FCSTD DOCUMENT  (FreeCAD 0.16R5861 (Git))
Label: flexystruder_body_holderV0.4
License: CreativeCommons Attribution-ShareAlike
LicenseURL: http://creativecommons.org/licenses/by-sa/4.0/
objects: Sketcher::SketchObject×9, PartDesign::Pad×6, Part::Feature×4, PartDesign::Pocket×3, Mesh::Feature×1, PartDesign::Chamfer×1, Part::Cut×1, PartDesign::Fillet×1
note: 34 computed .brp shape members not serialized (recipe doc carries the construction recipe); baked Part::Feature solids carry a one-line shape summary decoded from their .brp

FEATURE [Mesh::Feature] flexystruder_body_hex_v2_0  label="flexystruder_body_hex_v2.0"
FEATURE [Part::Feature] flexystruder_body_hex_v2_0001
  shape: bbox 97.06 x 64.55 x 27.5 mm, 7934 faces, 0 solids (baked)
FEATURE [Part::Feature] flexystruder_body_hex_v2_0001001  label="flexystruder_body_hex_v2_0002"
  shape: bbox 97.06 x 64.55 x 27.5 mm, 4378 faces, 0 solids (baked)
FEATURE [Part::Feature] flexystruder_body_hex_v2_0001001_solid  label="flexystruder_body_hex_v2_0002 (Solid)"
  shape: bbox 97.06 x 64.55 x 27.5 mm, 4378 faces (baked)
FEATURE [Sketcher::SketchObject] Sketch
  Placement = pos=(0,0,0) rot=(1,0,0;3.14159rad)
  Support = -> flexystruder_body_hex_v2_0001001_solid [Face1922]
  sketch-geometry (17):
    g0: ArcOfCircle CenterX=28 CenterY=-45.596 CenterZ=0 NormalX=0 NormalY=0 NormalZ=1 Radius=4.20615 StartAngle=4.71239 EndAngle=7.85398
    g1: ArcOfCircle CenterX=25 CenterY=-45.596 CenterZ=0 NormalX=0 NormalY=0 NormalZ=1 Radius=4.20615 StartAngle=1.5708 EndAngle=4.71239
    g2: LineSegment StartX=28 StartY=-41.3899 StartZ=0 EndX=25 EndY=-41.3899 EndZ=0
    g3: LineSegment StartX=28 StartY=-49.8022 StartZ=0 EndX=25 EndY=-49.8022 EndZ=0
    g4: ArcOfCircle CenterX=52.7327 CenterY=-58.2604 CenterZ=0 NormalX=0 NormalY=0 NormalZ=1 Radius=4.37439 StartAngle=1.5708 EndAngle=4.71239
    g5: ArcOfCircle CenterX=55.547 CenterY=-58.2604 CenterZ=0 NormalX=0 NormalY=0 NormalZ=1 Radius=4.37439 StartAngle=4.71239 EndAngle=7.85398
    g6: LineSegment StartX=52.7327 StartY=-62.6347 StartZ=0 EndX=55.547 EndY=-62.6347 EndZ=0
    g7: LineSegment StartX=52.7327 StartY=-53.886 StartZ=0 EndX=55.547 EndY=-53.886 EndZ=0
    g8: ArcOfCircle CenterX=41 CenterY=-17.6915 CenterZ=0 NormalX=0 NormalY=0 NormalZ=1 Radius=4.05397 StartAngle=4.71239 EndAngle=7.85398
    g9: ArcOfCircle CenterX=37.752 CenterY=-17.6915 CenterZ=0 NormalX=0 NormalY=0 NormalZ=1 Radius=4.05397 StartAngle=1.5708 EndAngle=4.71239
    g10: LineSegment StartX=41 StartY=-13.6375 StartZ=0 EndX=37.752 EndY=-13.6375 EndZ=0
    g11: LineSegment StartX=41 StartY=-21.7455 StartZ=0 EndX=37.752 EndY=-21.7455 EndZ=0
    g12: LineSegment StartX=23.6875 StartY=-6 StartZ=0 EndX=35.6731 EndY=-6 EndZ=0
    g13: LineSegment StartX=16.4026 StartY=-28 StartZ=0 EndX=28.3058 EndY=-28 EndZ=0
    g14: LineSegment StartX=28.3058 StartY=-28 StartZ=0 EndX=35.6731 EndY=-6 EndZ=0
    g15: LineSegment StartX=16.4026 StartY=-28 StartZ=0 EndX=16.4026 EndY=-12.5849 EndZ=0
    g16: ArcOfCircle CenterX=23.5917 CenterY=-13.2161 CenterZ=0 NormalX=0 NormalY=0 NormalZ=1 Radius=7.21677 StartAngle=1.55753 EndAngle=3.05401
  constraints (26):
    c: Tangent(g0,g3) = 1.5708
    c: Tangent(g0,g2) = -1.5708
    c: Tangent(g2,g1) = -1.5708
    c: Tangent(g3,g1) = 1.5708
    c: Horizontal(g2)
    c: Equal(g0,g1)
    c: Tangent(g4,g7) = 1.5708
    c: Tangent(g4,g6) = -1.5708
    c: Tangent(g6,g5) = -1.5708
    c: Tangent(g7,g5) = 1.5708
    c: Horizontal(g6)
    c: Equal(g4,g5)
    c: Tangent(g8,g11) = 1.5708
    c: Tangent(g8,g10) = -1.5708
    c: Tangent(g10,g9) = -1.5708
    c: Tangent(g11,g9) = 1.5708
    c: Horizontal(g10)
    c: Equal(g8,g9)
    c: Horizontal(g12)
    c: Horizontal(g13)
    c: Coincident(g14,g13)
    c: Coincident(g14,g12)
    c: Coincident(g15,g13)
    c: Vertical(g15)
    c: Coincident(g16,g12)
    c: Coincident(g16,g15)
FEATURE [PartDesign::Pad] Pad
  Length = 9.5
  Length2 = 100
  Reversed = true
  Sketch = -> Sketch
  Type = 0
FEATURE [Sketcher::SketchObject] Sketch001
  ExternalGeometry = -> [Pad]
  Placement = pos=(17.5,0,0) rot=(0.57735,0.57735,0.57735;2.0944rad)
  Support = -> Pad [Face375]
  sketch-geometry (4):
    g0: LineSegment StartX=26.5 StartY=12.5 StartZ=0 EndX=17.6702 EndY=12.5 EndZ=0
    g1: LineSegment StartX=17.6702 StartY=12.5 StartZ=0 EndX=17.6702 EndY=9.5 EndZ=0
    g2: LineSegment StartX=17.6702 StartY=9.5 StartZ=0 EndX=26.5 EndY=9.5 EndZ=0
    g3: LineSegment StartX=26.5 StartY=9.5 StartZ=0 EndX=26.5 EndY=12.5 EndZ=0
  constraints (10):
    c: Coincident(g0,g1)
    c: Coincident(g1,g2)
    c: Coincident(g2,g3)
    c: Coincident(g3,g0)
    c: Horizontal(g0)
    c: Horizontal(g2)
    c: Vertical(g1)
    c: Vertical(g3)
    c: Coincident(g0,g-4)
    c: PointOnObject(g1,g-3)
FEATURE [PartDesign::Pad] Pad001
  Length = 3
  Length2 = 100
  Sketch = -> Sketch001
  Type = 0
FEATURE [PartDesign::Chamfer] Chamfer
  Base = -> Pad001 [Edge1475]
  Size = 2.9
FEATURE [Sketcher::SketchObject] Sketch002
  ExternalGeometry = -> [Chamfer]
  Placement = pos=(0,0,27.5) rot=(0,0,1;0rad)
  Support = -> Chamfer [Face24]
  sketch-geometry (4):
    g0: LineSegment StartX=-6.5 StartY=48.2121 StartZ=0 EndX=-6.5 EndY=27.0119 EndZ=0
    g1: ArcOfCircle CenterX=3.84323 CenterY=38.0759 CenterZ=0 NormalX=0 NormalY=0 NormalZ=1 Radius=14.4819 StartAngle=0.364009 EndAngle=2.3663
    g2: LineSegment StartX=17.3762 StartY=43.2318 StartZ=0 EndX=17.5 EndY=37.4236 EndZ=0
    g3: ArcOfCircle CenterX=3.40646 CenterY=37.0436 CenterZ=0 NormalX=0 NormalY=0 NormalZ=1 Radius=14.0987 StartAngle=3.93327 EndAngle=6.31015
  constraints (10):
    c: Vertical(g0)
    c: Coincident(g0,g-5)
    c: Coincident(g0,g-6)
    c: Coincident(g1,g0)
    c: Coincident(g1,g-9)
    c: PointOnObject(g-21,g1)
    c: Coincident(g2,g1)
    c: Coincident(g2,g-7)
    c: Coincident(g3,g0)
    c: Coincident(g3,g2)
FEATURE [PartDesign::Pad] Pad002
  Length = 10
  Length2 = 100
  Reversed = true
  Sketch = -> Sketch002
  Type = 3
  UpToFace = -> Chamfer [Face709]
FEATURE [Sketcher::SketchObject] Sketch003
  ExternalGeometry = -> [Pad002]
  Placement = pos=(0,0,0) rot=(1,0,0;3.14159rad)
  Support = -> Pad002 [Face634]
  sketch-geometry (4):
    g0: LineSegment StartX=62.0584 StartY=-58.2729 StartZ=0 EndX=17.5 EndY=-58.2729 EndZ=0
    g1: LineSegment StartX=17.5 StartY=-58.2729 StartZ=0 EndX=17.5 EndY=-17.6702 EndZ=0
    g2: LineSegment StartX=17.5 StartY=-17.6702 StartZ=0 EndX=62.0584 EndY=-17.6702 EndZ=0
    g3: LineSegment StartX=62.0584 StartY=-17.6702 StartZ=0 EndX=62.0584 EndY=-58.2729 EndZ=0
  constraints (10):
    c: Coincident(g0,g1)
    c: Coincident(g1,g2)
    c: Coincident(g2,g3)
    c: Coincident(g3,g0)
    c: Horizontal(g0)
    c: Horizontal(g2)
    c: Vertical(g1)
    c: Vertical(g3)
    c: Coincident(g0,g-3)
    c: Coincident(g1,g-4)
FEATURE [PartDesign::Pad] Pad003
  Length = 9.5
  Length2 = 100
  Reversed = true
  Sketch = -> Sketch003
  Type = 0
FEATURE [Sketcher::SketchObject] Sketch004
  ExternalGeometry = -> [Pad003]
  Placement = pos=(0,0,0) rot=(1,0,0;3.14159rad)
  Support = -> Pad003 [Face456]
  sketch-geometry (4):
    g0: LineSegment StartX=16.4026 StartY=-12.5849 StartZ=0 EndX=-6.5 EndY=-12.5849 EndZ=0
    g1: LineSegment StartX=-6.5 StartY=-12.5849 StartZ=0 EndX=-6.5 EndY=-27.0119 EndZ=0
    g2: LineSegment StartX=-6.5 StartY=-27.0119 StartZ=0 EndX=16.4026 EndY=-27.0119 EndZ=0
    g3: LineSegment StartX=16.4026 StartY=-27.0119 StartZ=0 EndX=16.4026 EndY=-12.5849 EndZ=0
  constraints (10):
    c: Coincident(g0,g1)
    c: Coincident(g1,g2)
    c: Coincident(g2,g3)
    c: Coincident(g3,g0)
    c: Horizontal(g0)
    c: Horizontal(g2)
    c: Vertical(g1)
    c: Vertical(g3)
    c: Coincident(g0,g-4)
    c: Coincident(g1,g-3)
FEATURE [PartDesign::Pad] Pad004
  Length = 1
  Length2 = 100
  Reversed = true
  Sketch = -> Sketch004
  Type = 0
FEATURE [Part::Feature] Pad004001  label="Pad005"
  shape: bbox 97.06 x 64.55 x 27.5 mm, 2094 faces (baked)
FEATURE [Sketcher::SketchObject] Sketch005
  Placement = pos=(0,0,0) rot=(0.57735,0.57735,0.57735;2.0944rad)
  sketch-geometry (4):
    g0: LineSegment StartX=20 StartY=45 StartZ=0 EndX=75 EndY=45 EndZ=0
    g1: LineSegment StartX=75 StartY=45 StartZ=0 EndX=75 EndY=-25 EndZ=0
    g2: LineSegment StartX=75 StartY=-25 StartZ=0 EndX=20 EndY=-25 EndZ=0
    g3: LineSegment StartX=20 StartY=-25 StartZ=0 EndX=20 EndY=45 EndZ=0
  constraints (12):
    c: Coincident(g0,g1)
    c: Coincident(g1,g2)
    c: Coincident(g2,g3)
    c: Coincident(g3,g0)
    c: Horizontal(g0)
    c: Horizontal(g2)
    c: Vertical(g1)
    c: Vertical(g3)
    c: DistanceY(g1) = -70
    c: DistanceY(g-1,g2) = -25
    c: DistanceX(g-1,g1) = 75
    c: DistanceX(g2) = -55
FEATURE [PartDesign::Pad] Pad004002
  Length = 130
  Length2 = 20
  Placement = pos=(0,0,0) rot=(0.57735,0.57735,0.57735;2.0944rad)
  Sketch = -> Sketch005
  Type = 4
FEATURE [Part::Cut] Cut
  Base = -> Pad004002
  Tool = -> Pad004001
FEATURE [Sketcher::SketchObject] Sketch006
  ExternalGeometry = -> [Cut]
  Placement = pos=(0,0,45) rot=(0,0,1;0rad)
  Support = -> Cut [Face1]
  sketch-geometry (3):
    g0: ArcOfCircle CenterX=66.7062 CenterY=83.914 CenterZ=0 NormalX=0 NormalY=0 NormalZ=1 Radius=63.9184 StartAngle=4.72413 EndAngle=6.14327
    g1: LineSegment StartX=130 StartY=75 StartZ=0 EndX=130 EndY=20 EndZ=0
    g2: LineSegment StartX=130 StartY=20 StartZ=0 EndX=67.4569 EndY=20 EndZ=0
  constraints (8):
    c: Coincident(g1,g0)
    c: Coincident(g1,g-4)
    c: Vertical(g1)
    c: Coincident(g2,g1)
    c: Coincident(g2,g0)
    c: Horizontal(g2)
    c: Coincident(g0,g-3)
    c: Coincident(g1,g-3)
FEATURE [PartDesign::Pocket] Pocket
  Length = 5
  Sketch = -> Sketch006
  Type = 1
FEATURE [PartDesign::Fillet] Fillet
  Base = -> Pocket [Edge3,Edge4,Edge1,Edge7,Edge6,Edge10,Edge12]
  Radius = 10
FEATURE [Sketcher::SketchObject] Sketch007
  Placement = pos=(0,20,0) rot=(1,0,0;1.5708rad)
  Support = -> Fillet [Face12]
  sketch-geometry (1):
    g0: Circle CenterX=0.551868 CenterY=14.0293 CenterZ=0 NormalX=0 NormalY=0 NormalZ=1 Radius=4
  constraints (1):
    c: Radius(g0) = 4
FEATURE [PartDesign::Pocket] Pocket001
  Length = 5
  Sketch = -> Sketch007
  Type = 1
FEATURE [Sketcher::SketchObject] Sketch008
  Placement = pos=(0,75,0) rot=(0,0.707107,0.707107;3.14159rad)
  Support = -> Pocket001 [Face2]
  sketch-geometry (4):
    g0: LineSegment StartX=-120 StartY=35 StartZ=0 EndX=-75 EndY=35 EndZ=0
    g1: LineSegment StartX=-75 StartY=35 StartZ=0 EndX=-75 EndY=-15 EndZ=0
    g2: LineSegment StartX=-75 StartY=-15 StartZ=0 EndX=-120 EndY=-15 EndZ=0
    g3: LineSegment StartX=-120 StartY=-15 StartZ=0 EndX=-120 EndY=35 EndZ=0
  constraints (8):
    c: Coincident(g0,g1)
    c: Coincident(g1,g2)
    c: Coincident(g2,g3)
    c: Coincident(g3,g0)
    c: Horizontal(g0)
    c: Horizontal(g2)
    c: Vertical(g1)
    c: Vertical(g3)
FEATURE [PartDesign::Pocket] Pocket002
  Length = 5
  Sketch = -> Sketch008
  Type = 1
